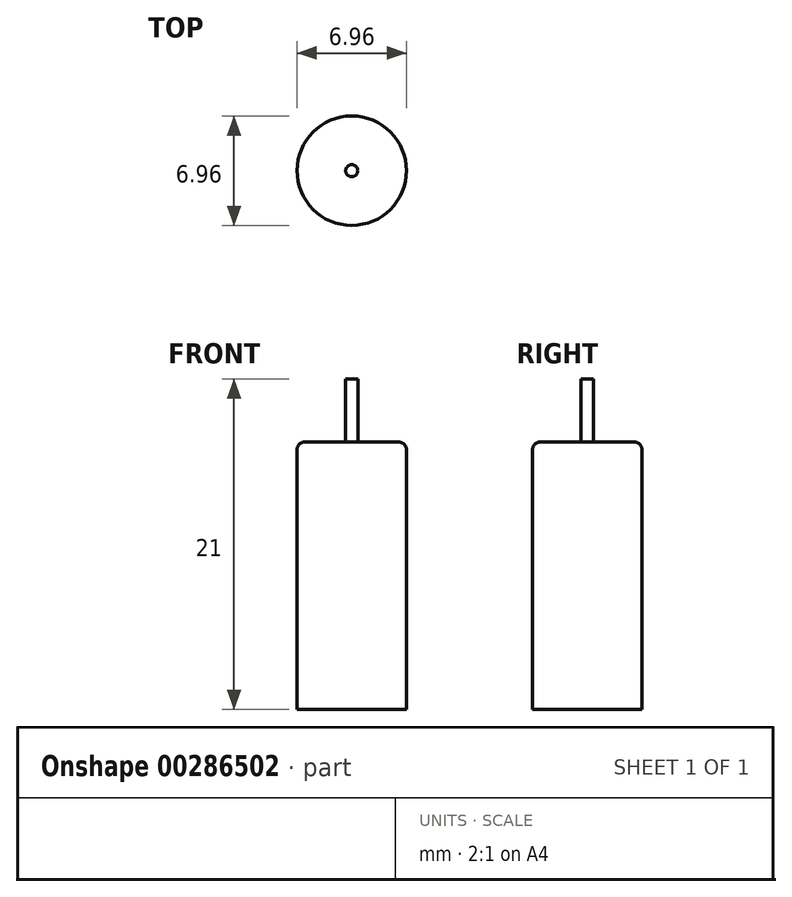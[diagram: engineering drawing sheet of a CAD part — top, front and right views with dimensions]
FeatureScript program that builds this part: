
annotation { "Feature Type Name" : "Feature", "Feature Type Description" : "" }
export const myFeature = defineFeature(function(context is Context, id is Id, definition is map)
    precondition{}
    {
        {
            var Q0;
            Q0=qCreatedBy(makeId("Top.planeOp"),FACE);
            var sketch = newSketch(context, id + "F0", { "sketchPlane" : qUnion([Q0])});
            skCircle(sketch, "E0", {"center": v(0, 0) * mm, "radius": 3.47 * mm});
            skSolve(sketch);
        }
        {
            var Q0;
            Q0 = qSketchRegion(id + "F0", true);
            extrude(context, id + "F1", {"entities" : qUnion([Q0]), "depth" : 17 * mm, "offsetDistance" : 25 * mm});
        }
        {
            var Q0;
            Q0=makeQuery(id+"F1.opExtrude","CAP_FACE",FACE,{"disambiguationData":[OSD([sQuery(id+"F0.wireOp",EDGE,"E0")])],"isStart":false});
            var sketch = newSketch(context, id + "F2", { "sketchPlane" : qUnion([Q0])});
            skCircle(sketch, "E1", {"center": v(0, 0) * mm, "radius": 0.39 * mm});
            skSolve(sketch);
        }
        {
            var Q0;
            Q0 = qSketchRegion(id + "F2", true);
            extrude(context, id + "F3", {"entities" : qUnion([Q0]), "depth" : 4 * mm, "offsetDistance" : 25 * mm});
        }
        {
            var Q0;
            Q0=makeQuery(id+"F1.opExtrude","CAP_EDGE",EDGE,{"disambiguationData":[OSD([sQuery(id+"F0.wireOp",EDGE,"E0")])],"isStart":false});
            fillet(context, id + "F4", {"entities" : qUnion([Q0]), "radius" : .5 * mm, "tangentPropagation" : true, "allowEdgeOverflow" : false});
        }
    });
